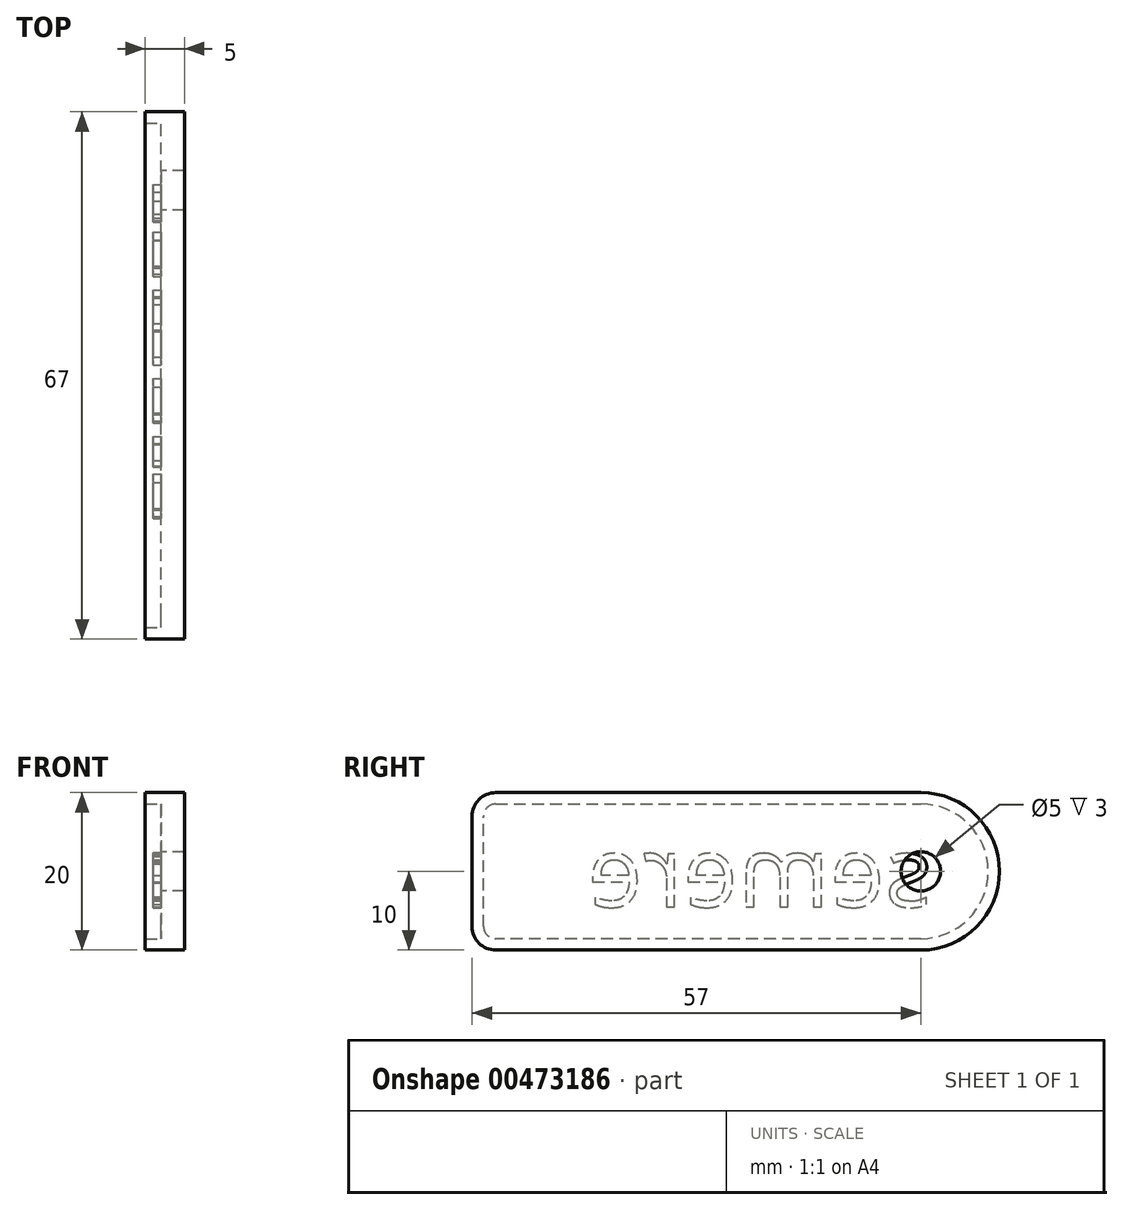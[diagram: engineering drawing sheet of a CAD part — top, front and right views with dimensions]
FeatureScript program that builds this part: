
annotation { "Feature Type Name" : "Feature", "Feature Type Description" : "" }
export const myFeature = defineFeature(function(context is Context, id is Id, definition is map)
    precondition{}
    {
        {
            var Q0;
            Q0=qCreatedBy(makeId("Right.planeOp"),FACE);
            var sketch = newSketch(context, id + "F0", { "sketchPlane" : qUnion([Q0])});
            skLineSegment(sketch, "E0.bottom", {"start": v(-30.5, -10) * mm, "end": v(23.5, -10) * mm});
            skLineSegment(sketch, "E0.top", {"start": v(-30.5, 10) * mm, "end": v(23.5, 10) * mm});
            skLineSegment(sketch, "E0.left", {"start": v(-33.5, 7) * mm, "end": v(-33.5, -7) * mm});
            skArc(sketch, "E1", {"start": v(23.5, -10) * mm, "mid": v(33.5, 0) * mm, "end": v(23.5, 10) * mm});
            skArc(sketch, "E2", {"start": v(-30.5, 10) * mm, "mid": v(-32.62, 9.12) * mm, "end": v(-33.5, 7) * mm});
            skArc(sketch, "E3", {"start": v(-33.5, -7) * mm, "mid": v(-32.62, -9.12) * mm, "end": v(-30.5, -10) * mm});
            skCircle(sketch, "E4", {"center": v(23.5, 0) * mm, "radius": 2.5 * mm});
            skLineSegment(sketch, "E5", {"start": v(33.5, 65.23) * mm, "end": v(33.5, -25.1) * mm, "construction": true});
            skSolve(sketch);
        }
        {
            var Q0;
            Q0=makeQuery(id+"F0.imprint","IMPRINT",FACE,{"disambiguationData":[TD([[makeQuery(id+"F0.imprint","IMPRINT",EDGE,{"derivedFrom":sQuery(id+"F0.wireOp",EDGE,"E0.bottom")}),1.0]])]});
            extrude(context, id + "F1", {"entities" : qUnion([Q0]), "depth" : 3 * mm});
        }
        {
            var Q0;
            Q0=makeQuery(id+"F1.opExtrude","CAP_FACE",FACE,{"disambiguationData":[OSD([sQuery(id+"F0.wireOp",EDGE,"E0.bottom"),sQuery(id+"F0.wireOp",EDGE,"E0.top"),sQuery(id+"F0.wireOp",EDGE,"E0.left"),sQuery(id+"F0.wireOp",EDGE,"E1"),sQuery(id+"F0.wireOp",EDGE,"E2"),sQuery(id+"F0.wireOp",EDGE,"E3"),sQuery(id+"F0.wireOp",EDGE,"E4")])],"isStart":true});
            var sketch = newSketch(context, id + "F2", { "sketchPlane" : qUnion([Q0])});
            skText(sketch, "E6", { "text": "semere", "fontName": "OpenSans-Regular.ttf"});
            const initialGuessF2  = {"E6": [-0.0249, -0.0045, 1, 0, 0.009]};
            skSetInitialGuess(sketch, initialGuessF2);
            skSolve(sketch);
        }
        {
            var Q0;
            Q0 = qSketchRegion(id + "F2", true);
            extrude(context, id + "F3", {"entities" : qUnion([Q0]), "operationType" : NewBodyOperationType.ADD, "depth" : 1 * mm});
        }
        {
            var Q0;
            {var subQ0=sQuery(id+"F0.wireOp",EDGE,"E0.left");var subQ1=sQuery(id+"F0.wireOp",EDGE,"E4");var subQ2=sQuery(id+"F0.wireOp",EDGE,"E3");var subQ3=sQuery(id+"F0.wireOp",EDGE,"E2");var subQ4=sQuery(id+"F0.wireOp",EDGE,"E0.bottom");var subQ5=sQuery(id+"F0.wireOp",EDGE,"E1");var subQ6=sQuery(id+"F0.wireOp",EDGE,"E0.top");Q0=makeQuery(id+"F3.boolean.opBoolean","SPLIT",FACE,{"disambiguationData":[TD([makeQuery(id+"F1.opExtrude","SWEPT_FACE",FACE,{"disambiguationData":[OSD([subQ4])]})])],"derivedFrom":makeQuery(id+"F1.opExtrude","CAP_FACE",FACE,{"disambiguationData":[OSD([subQ4,subQ6,subQ0,subQ5,subQ3,subQ2,subQ1])],"isStart":true})});}
            var sketch = newSketch(context, id + "F4", { "sketchPlane" : qUnion([Q0])});
            skArc(sketch, "E7.0", {"start": v(32.05, 7) * mm, "mid": v(31.6, 8.1) * mm, "end": v(30.5, 8.55) * mm});
            skArc(sketch, "E7.1", {"start": v(-23.5, 8.55) * mm, "mid": v(-32.05, 0) * mm, "end": v(-23.5, -8.55) * mm});
            skLineSegment(sketch, "E7.2", {"start": v(-23.5, -8.55) * mm, "end": v(30.5, -8.55) * mm});
            skLineSegment(sketch, "E7.3", {"start": v(30.5, 8.55) * mm, "end": v(-23.5, 8.55) * mm});
            skArc(sketch, "E7.4", {"start": v(30.5, -8.55) * mm, "mid": v(31.6, -8.1) * mm, "end": v(32.05, -7) * mm});
            skLineSegment(sketch, "E7.5", {"start": v(32.05, -7) * mm, "end": v(32.05, 7) * mm});
            skSolve(sketch);
        }
        {
            var Q0;
            Q0=makeQuery(id+"F4.imprint","IMPRINT",FACE,{"disambiguationData":[TD([[makeQuery(id+"F4.imprint","IMPRINT",EDGE,{"derivedFrom":sQuery(id+"F4.wireOp",EDGE,"E7.0")}),-1.0]])]});
            extrude(context, id + "F5", {"entities" : qUnion([Q0]), "operationType" : NewBodyOperationType.ADD, "depth" : 2 * mm});
        }
    });
